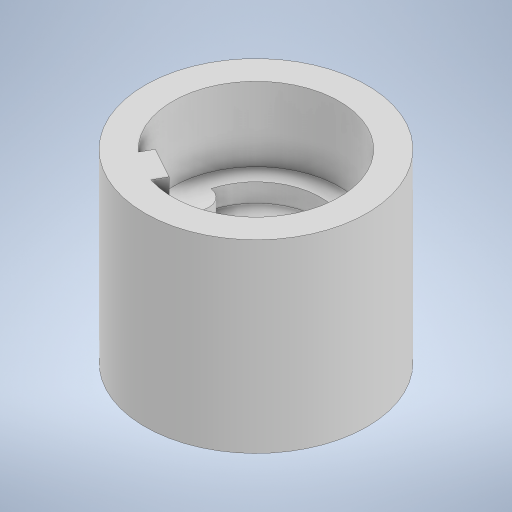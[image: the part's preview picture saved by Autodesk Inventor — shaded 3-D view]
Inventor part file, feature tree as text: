
AUTODESK INVENTOR PART (.ipt)
format: ipt  version: 2023 (Build 270158000, 158)  size: 249,856 bytes
history: native  units: mm
features: extrude x4, sketch x4, other x1
ambient origin geometry x8: Origin, YZ Plane, XZ Plane, XY Plane, X Axis, Y Axis, Z Axis, Center Point
bodies: Body1 (feature_tree)
feature tree (9):
  other  "Твердое тело1"
  extrude  "Выдавливание1"  Depth=7.0mm
  extrude  "Выдавливание2"  Depth=1.9mm
  extrude  "Выдавливание3"  Depth=30.0mm TaperAngle=360.0deg
  extrude  "Выдавливание4"  Depth=9.0mm
  sketch  "Эскиз1"
  sketch  "Эскиз2"
  sketch  "Эскиз3"
  sketch  "Эскиз4"
